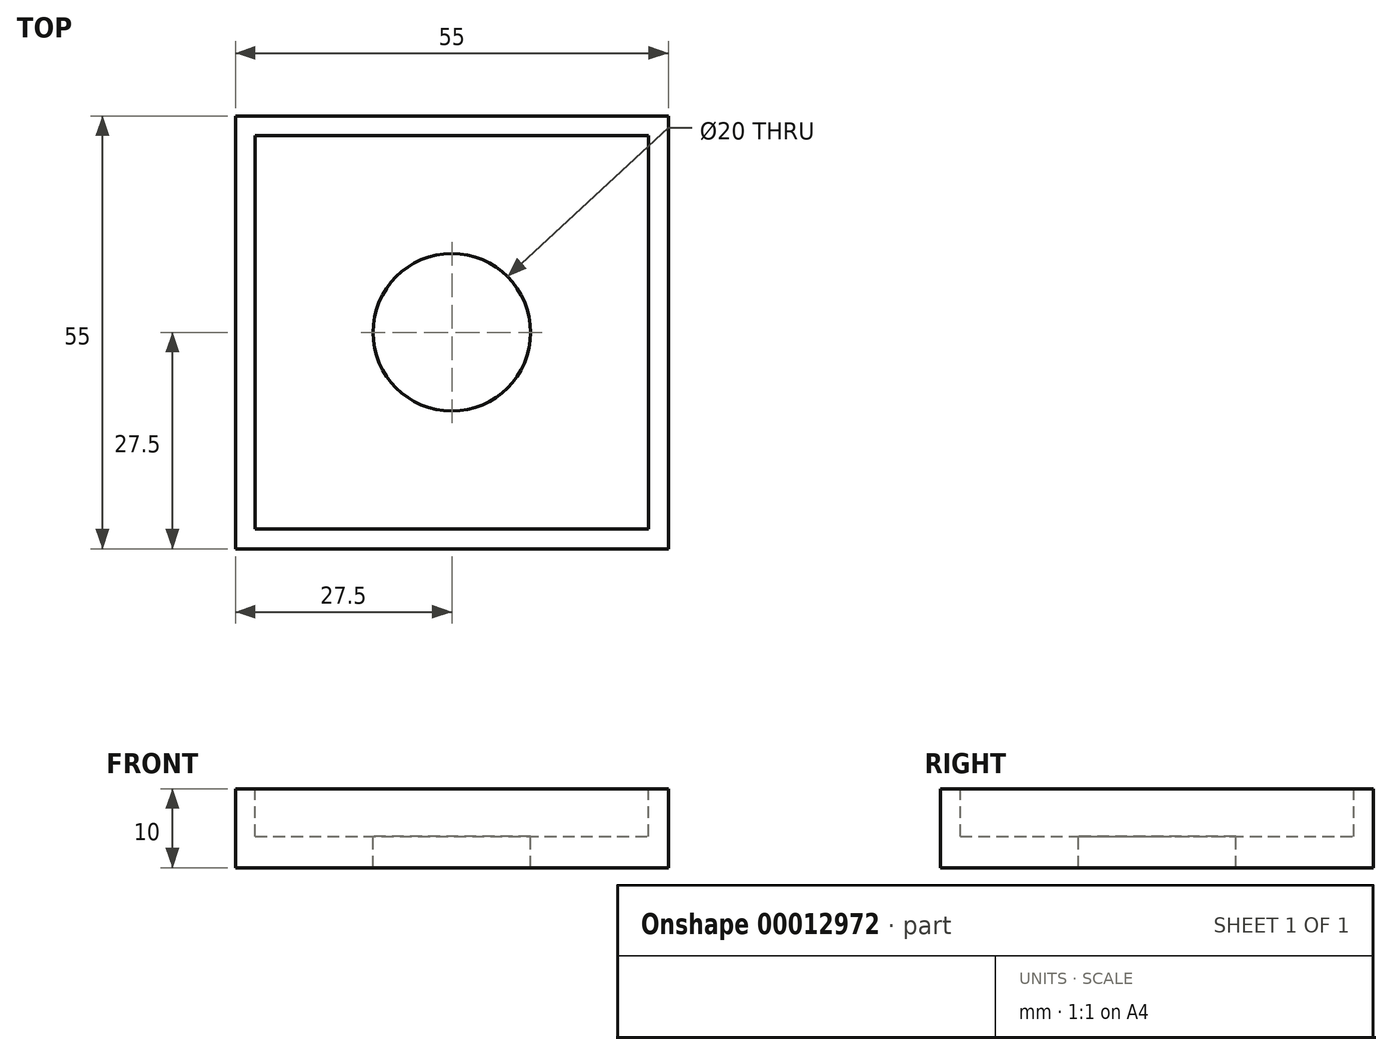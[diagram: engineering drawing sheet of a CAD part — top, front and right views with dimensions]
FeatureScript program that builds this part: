
annotation { "Feature Type Name" : "Feature", "Feature Type Description" : "" }
export const myFeature = defineFeature(function(context is Context, id is Id, definition is map)
    precondition{}
    {
        {
            var Q0;
            Q0=qCreatedBy(makeId("Top.planeOp"),FACE);
            var sketch = newSketch(context, id + "F0", { "sketchPlane" : qUnion([Q0])});
            skLineSegment(sketch, "E0.rect.bottom", {"start": v(-27.5, 27.5) * mm, "end": v(27.5, 27.5) * mm});
            skLineSegment(sketch, "E0.rect.top", {"start": v(-27.5, -27.5) * mm, "end": v(27.5, -27.5) * mm});
            skLineSegment(sketch, "E0.rect.left", {"start": v(-27.5, 27.5) * mm, "end": v(-27.5, -27.5) * mm});
            skLineSegment(sketch, "E0.rect.right", {"start": v(27.5, 27.5) * mm, "end": v(27.5, -27.5) * mm});
            skPoint(sketch, "E0.rect.middle", {"position": v(0, 0) * mm});
            skSolve(sketch);
        }
        {
            var Q0;
            Q0 = qSketchRegion(id + "F0", true);
            extrude(context, id + "F1", {"entities" : qUnion([Q0]), "depth" : 10 * mm});
        }
        {
            var Q0;
            Q0=makeQuery(id+"F1.opExtrude","CAP_FACE",FACE,{"disambiguationData":[OSD([sQuery(id+"F0.wireOp",EDGE,"E0.rect.bottom"),sQuery(id+"F0.wireOp",EDGE,"E0.rect.top"),sQuery(id+"F0.wireOp",EDGE,"E0.rect.left"),sQuery(id+"F0.wireOp",EDGE,"E0.rect.right")])],"isStart":false});
            var sketch = newSketch(context, id + "F2", { "sketchPlane" : qUnion([Q0])});
            skLineSegment(sketch, "E1.rect.bottom", {"start": v(-25, -25) * mm, "end": v(25, -25) * mm});
            skLineSegment(sketch, "E1.rect.top", {"start": v(-25, 25) * mm, "end": v(25, 25) * mm});
            skLineSegment(sketch, "E1.rect.left", {"start": v(-25, -25) * mm, "end": v(-25, 25) * mm});
            skLineSegment(sketch, "E1.rect.right", {"start": v(25, -25) * mm, "end": v(25, 25) * mm});
            skPoint(sketch, "E1.rect.middle", {"position": v(0, 0) * mm});
            skSolve(sketch);
        }
        {
            var Q0;
            Q0 = qSketchRegion(id + "F2", true);
            extrude(context, id + "F3", {"entities" : qUnion([Q0]), "operationType" : NewBodyOperationType.REMOVE, "oppositeDirection" : true, "depth" : 6 * mm});
        }
        {
            var Q0;
            Q0=makeQuery(id+"F3.boolean.opBoolean","COPY",FACE,{"derivedFrom":makeQuery(id+"F3.opExtrude","CAP_FACE",FACE,{"disambiguationData":[OSD([sQuery(id+"F2.wireOp",EDGE,"E1.rect.bottom"),sQuery(id+"F2.wireOp",EDGE,"E1.rect.top"),sQuery(id+"F2.wireOp",EDGE,"E1.rect.left"),sQuery(id+"F2.wireOp",EDGE,"E1.rect.right")])],"isStart":false})});
            var sketch = newSketch(context, id + "F4", { "sketchPlane" : qUnion([Q0])});
            skCircle(sketch, "E2", {"center": v(0, 0) * mm, "radius": 10 * mm});
            skSolve(sketch);
        }
        {
            var Q0;
            Q0 = qSketchRegion(id + "F4", true);
            extrude(context, id + "F5", {"entities" : qUnion([Q0]), "operationType" : NewBodyOperationType.REMOVE, "endBound" : BoundingType.UP_TO_NEXT, "oppositeDirection" : true, "depth" : 25 * mm});
        }
    });
